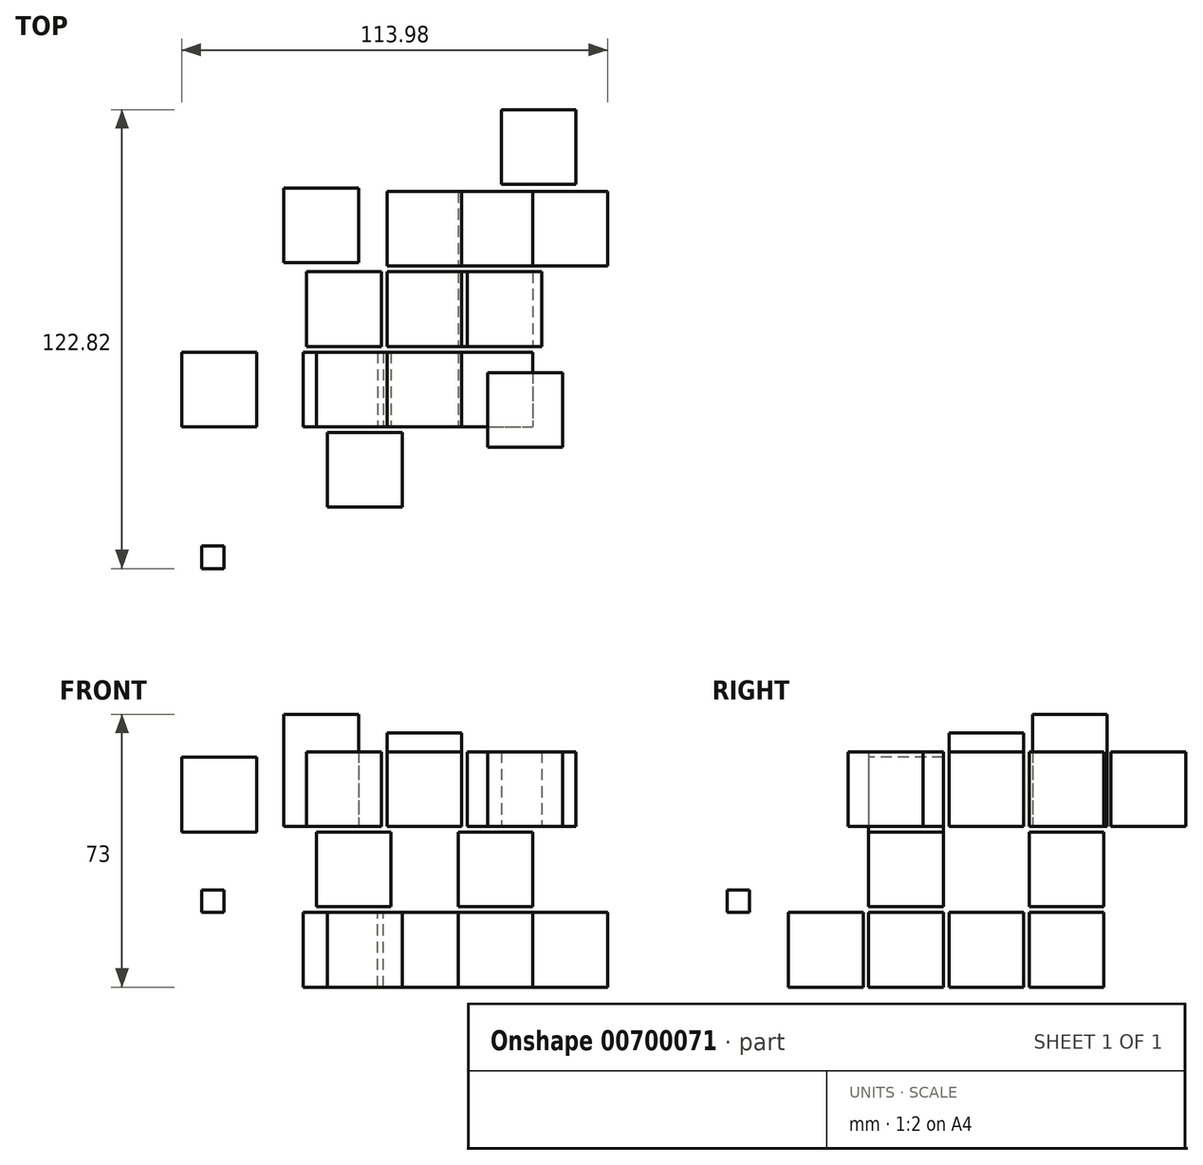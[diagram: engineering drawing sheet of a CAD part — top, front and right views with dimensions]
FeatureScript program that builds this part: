
annotation { "Feature Type Name" : "Feature", "Feature Type Description" : "" }
export const myFeature = defineFeature(function(context is Context, id is Id, definition is map)
    precondition{}
    {
        {
            var Q0;
            Q0=qCreatedBy(makeId("Top.planeOp"),FACE);
            var sketch = newSketch(context, id + "F0", { "sketchPlane" : qUnion([Q0])});
            skLineSegment(sketch, "E0.bottom", {"start": v(-9, -26) * mm, "end": v(11, -26) * mm});
            skLineSegment(sketch, "E0.top", {"start": v(-9, -46) * mm, "end": v(11, -46) * mm});
            skLineSegment(sketch, "E0.left", {"start": v(-9, -26) * mm, "end": v(-9, -46) * mm});
            skLineSegment(sketch, "E0.right", {"start": v(11, -26) * mm, "end": v(11, -46) * mm});
            skLineSegment(sketch, "E1.bottom", {"start": v(-15.53, -4.5) * mm, "end": v(4.47, -4.5) * mm});
            skLineSegment(sketch, "E1.top", {"start": v(-15.53, -24.5) * mm, "end": v(4.47, -24.5) * mm});
            skLineSegment(sketch, "E1.left", {"start": v(-15.53, -4.5) * mm, "end": v(-15.53, -24.5) * mm});
            skLineSegment(sketch, "E1.right", {"start": v(4.47, -4.5) * mm, "end": v(4.47, -24.5) * mm});
            skLineSegment(sketch, "E2.bottom", {"start": v(5.97, -4.5) * mm, "end": v(25.97, -4.5) * mm});
            skLineSegment(sketch, "E2.top", {"start": v(5.97, -24.5) * mm, "end": v(25.97, -24.5) * mm});
            skLineSegment(sketch, "E2.left", {"start": v(5.97, -4.5) * mm, "end": v(5.97, -24.5) * mm});
            skLineSegment(sketch, "E2.right", {"start": v(25.97, -4.5) * mm, "end": v(25.97, -24.5) * mm});
            skLineSegment(sketch, "E3.bottom", {"start": v(25.97, 17) * mm, "end": v(45.97, 17) * mm});
            skLineSegment(sketch, "E3.top", {"start": v(25.97, -3) * mm, "end": v(45.97, -3) * mm});
            skLineSegment(sketch, "E3.left", {"start": v(25.97, 17) * mm, "end": v(25.97, -3) * mm});
            skLineSegment(sketch, "E3.right", {"start": v(45.97, 17) * mm, "end": v(45.97, -3) * mm});
            skLineSegment(sketch, "E4.bottom", {"start": v(45.97, 38.5) * mm, "end": v(65.97, 38.5) * mm});
            skLineSegment(sketch, "E4.top", {"start": v(45.97, 18.5) * mm, "end": v(65.97, 18.5) * mm});
            skLineSegment(sketch, "E4.left", {"start": v(45.97, 38.5) * mm, "end": v(45.97, 18.5) * mm});
            skLineSegment(sketch, "E4.right", {"start": v(65.97, 38.5) * mm, "end": v(65.97, 18.5) * mm});
            skSolve(sketch);
        }
        {
            var Q0;
            Q0=makeQuery(id+"F0.imprint","IMPRINT",FACE,{"disambiguationData":[TD([[makeQuery(id+"F0.imprint","IMPRINT",EDGE,{"derivedFrom":sQuery(id+"F0.wireOp",EDGE,"E0.bottom")}),-1.0]])]});
            var Q1;
            Q1=makeQuery(id+"F0.imprint","IMPRINT",FACE,{"disambiguationData":[TD([[makeQuery(id+"F0.imprint","IMPRINT",EDGE,{"derivedFrom":sQuery(id+"F0.wireOp",EDGE,"E1.bottom")}),-1.0]])]});
            var Q2;
            Q2=makeQuery(id+"F0.imprint","IMPRINT",FACE,{"disambiguationData":[TD([[makeQuery(id+"F0.imprint","IMPRINT",EDGE,{"derivedFrom":sQuery(id+"F0.wireOp",EDGE,"E2.bottom")}),-1.0]])]});
            var Q3;
            Q3=makeQuery(id+"F0.imprint","IMPRINT",FACE,{"disambiguationData":[TD([[makeQuery(id+"F0.imprint","IMPRINT",EDGE,{"derivedFrom":sQuery(id+"F0.wireOp",EDGE,"E3.bottom")}),-1.0]])]});
            var Q4;
            Q4=makeQuery(id+"F0.imprint","IMPRINT",FACE,{"disambiguationData":[TD([[makeQuery(id+"F0.imprint","IMPRINT",EDGE,{"derivedFrom":sQuery(id+"F0.wireOp",EDGE,"E4.bottom")}),-1.0]])]});
            extrude(context, id + "F1", {"entities" : qUnion([Q0, Q1, Q2, Q3, Q4]), "oppositeDirection" : true, "depth" : 20 * mm, "offsetDistance" : 25 * mm});
        }
        {
            var Q0;
            Q0=makeQuery(id+"F1.opExtrude","CAP_FACE",FACE,{"disambiguationData":[OSD([sQuery(id+"F0.wireOp",EDGE,"E0.bottom"),sQuery(id+"F0.wireOp",EDGE,"E0.top"),sQuery(id+"F0.wireOp",EDGE,"E0.left"),sQuery(id+"F0.wireOp",EDGE,"E0.right")])],"isStart":true});
            cPlane(context, id + "F2", {"entities" : qUnion([Q0]), "cplaneType" : CPlaneType.OFFSET, "offset" : 1.5 * mm, "width" : 150 * mm, "height" : 150 * mm});
        }
        {
            var Q0;
            Q0=qCreatedBy(id+"F2.planeOp",FACE);
            var sketch = newSketch(context, id + "F3", { "sketchPlane" : qUnion([Q0])});
            skLineSegment(sketch, "E5.bottom", {"start": v(-12, -4.5) * mm, "end": v(8, -4.5) * mm});
            skLineSegment(sketch, "E5.top", {"start": v(-12, -24.5) * mm, "end": v(8, -24.5) * mm});
            skLineSegment(sketch, "E5.left", {"start": v(-12, -4.5) * mm, "end": v(-12, -24.5) * mm});
            skLineSegment(sketch, "E5.right", {"start": v(8, -4.5) * mm, "end": v(8, -24.5) * mm});
            skLineSegment(sketch, "E6.bottom", {"start": v(25.97, -4.5) * mm, "end": v(45.97, -4.5) * mm});
            skLineSegment(sketch, "E6.top", {"start": v(25.97, -24.5) * mm, "end": v(45.97, -24.5) * mm});
            skLineSegment(sketch, "E6.left", {"start": v(25.97, -4.5) * mm, "end": v(25.97, -24.5) * mm});
            skLineSegment(sketch, "E6.right", {"start": v(45.97, -4.5) * mm, "end": v(45.97, -24.5) * mm});
            skLineSegment(sketch, "E7.bottom", {"start": v(25.97, 38.5) * mm, "end": v(45.97, 38.5) * mm});
            skLineSegment(sketch, "E7.top", {"start": v(25.97, 18.5) * mm, "end": v(45.97, 18.5) * mm});
            skLineSegment(sketch, "E7.left", {"start": v(25.97, 38.5) * mm, "end": v(25.97, 18.5) * mm});
            skLineSegment(sketch, "E7.right", {"start": v(45.97, 38.5) * mm, "end": v(45.97, 18.5) * mm});
            skSolve(sketch);
        }
        {
            var Q0;
            Q0=makeQuery(id+"F3.imprint","IMPRINT",FACE,{"disambiguationData":[TD([[makeQuery(id+"F3.imprint","IMPRINT",EDGE,{"derivedFrom":sQuery(id+"F3.wireOp",EDGE,"E5.bottom")}),-1.0]])]});
            var Q1;
            Q1=makeQuery(id+"F3.imprint","IMPRINT",FACE,{"disambiguationData":[TD([[makeQuery(id+"F3.imprint","IMPRINT",EDGE,{"derivedFrom":sQuery(id+"F3.wireOp",EDGE,"E6.bottom")}),-1.0]])]});
            var Q2;
            Q2=makeQuery(id+"F3.imprint","IMPRINT",FACE,{"disambiguationData":[TD([[makeQuery(id+"F3.imprint","IMPRINT",EDGE,{"derivedFrom":sQuery(id+"F3.wireOp",EDGE,"E7.bottom")}),-1.0]])]});
            extrude(context, id + "F4", {"entities" : qUnion([Q0, Q1, Q2]), "operationType" : NewBodyOperationType.ADD, "depth" : 20 * mm, "offsetDistance" : 25 * mm});
        }
        {
            var Q0;
            Q0=makeQuery(id+"F4.opExtrude","CAP_FACE",FACE,{"disambiguationData":[OSD([sQuery(id+"F3.wireOp",EDGE,"E6.bottom"),sQuery(id+"F3.wireOp",EDGE,"E6.top"),sQuery(id+"F3.wireOp",EDGE,"E6.left"),sQuery(id+"F3.wireOp",EDGE,"E6.right")])],"isStart":false});
            cPlane(context, id + "F5", {"entities" : qUnion([Q0]), "cplaneType" : CPlaneType.OFFSET, "offset" : 1.5 * mm, "width" : 150 * mm, "height" : 150 * mm});
        }
        {
            var Q0;
            Q0=qCreatedBy(id+"F5.planeOp",FACE);
            var sketch = newSketch(context, id + "F6", { "sketchPlane" : qUnion([Q0])});
            skLineSegment(sketch, "E8.bottom", {"start": v(6.9, -4.5) * mm, "end": v(26.9, -4.5) * mm});
            skLineSegment(sketch, "E8.top", {"start": v(6.9, -24.5) * mm, "end": v(26.9, -24.5) * mm});
            skLineSegment(sketch, "E8.left", {"start": v(6.9, -4.5) * mm, "end": v(6.9, -24.5) * mm});
            skLineSegment(sketch, "E8.right", {"start": v(26.9, -4.5) * mm, "end": v(26.9, -24.5) * mm});
            skLineSegment(sketch, "E9.bottom", {"start": v(33.9, -10) * mm, "end": v(53.9, -10) * mm});
            skLineSegment(sketch, "E9.top", {"start": v(33.9, -30) * mm, "end": v(53.9, -30) * mm});
            skLineSegment(sketch, "E9.left", {"start": v(33.9, -10) * mm, "end": v(33.9, -30) * mm});
            skLineSegment(sketch, "E9.right", {"start": v(53.9, -10) * mm, "end": v(53.9, -30) * mm});
            skLineSegment(sketch, "E10.bottom", {"start": v(28.4, 17) * mm, "end": v(48.4, 17) * mm});
            skLineSegment(sketch, "E10.top", {"start": v(28.4, -3) * mm, "end": v(48.4, -3) * mm});
            skLineSegment(sketch, "E10.left", {"start": v(28.4, 17) * mm, "end": v(28.4, -3) * mm});
            skLineSegment(sketch, "E10.right", {"start": v(48.4, 17) * mm, "end": v(48.4, -3) * mm});
            skLineSegment(sketch, "E11.bottom", {"start": v(6.9, 17) * mm, "end": v(26.9, 17) * mm});
            skLineSegment(sketch, "E11.top", {"start": v(6.9, -3) * mm, "end": v(26.9, -3) * mm});
            skLineSegment(sketch, "E11.left", {"start": v(6.9, 17) * mm, "end": v(6.9, -3) * mm});
            skLineSegment(sketch, "E11.right", {"start": v(26.9, 17) * mm, "end": v(26.9, -3) * mm});
            skLineSegment(sketch, "E12.bottom", {"start": v(6.9, 38.5) * mm, "end": v(26.9, 38.5) * mm});
            skLineSegment(sketch, "E12.top", {"start": v(6.9, 18.5) * mm, "end": v(26.9, 18.5) * mm});
            skLineSegment(sketch, "E12.left", {"start": v(6.9, 38.5) * mm, "end": v(6.9, 18.5) * mm});
            skLineSegment(sketch, "E12.right", {"start": v(26.9, 38.5) * mm, "end": v(26.9, 18.5) * mm});
            skLineSegment(sketch, "E13.bottom", {"start": v(-14.6, 17) * mm, "end": v(5.4, 17) * mm});
            skLineSegment(sketch, "E13.top", {"start": v(-14.6, -3) * mm, "end": v(5.4, -3) * mm});
            skLineSegment(sketch, "E13.left", {"start": v(-14.6, 17) * mm, "end": v(-14.6, -3) * mm});
            skLineSegment(sketch, "E13.right", {"start": v(5.4, 17) * mm, "end": v(5.4, -3) * mm});
            skLineSegment(sketch, "E14.bottom", {"start": v(37.52, 60.38) * mm, "end": v(57.52, 60.38) * mm});
            skLineSegment(sketch, "E14.top", {"start": v(37.52, 40.38) * mm, "end": v(57.52, 40.38) * mm});
            skLineSegment(sketch, "E14.left", {"start": v(37.52, 60.38) * mm, "end": v(37.52, 40.38) * mm});
            skLineSegment(sketch, "E14.right", {"start": v(57.52, 60.38) * mm, "end": v(57.52, 40.38) * mm});
            skLineSegment(sketch, "E15.bottom", {"start": v(-20.71, 39.39) * mm, "end": v(-0.71, 39.39) * mm});
            skLineSegment(sketch, "E15.top", {"start": v(-20.71, 19.39) * mm, "end": v(-0.71, 19.39) * mm});
            skLineSegment(sketch, "E15.left", {"start": v(-20.71, 39.39) * mm, "end": v(-20.71, 19.39) * mm});
            skLineSegment(sketch, "E15.right", {"start": v(-0.71, 39.39) * mm, "end": v(-0.71, 19.39) * mm});
            skSolve(sketch);
        }
        {
            var Q0;
            Q0=makeQuery(id+"F6.imprint","IMPRINT",FACE,{"disambiguationData":[TD([[makeQuery(id+"F6.imprint","IMPRINT",EDGE,{"derivedFrom":sQuery(id+"F6.wireOp",EDGE,"E9.bottom")}),-1.0]])]});
            var Q1;
            Q1=makeQuery(id+"F6.imprint","IMPRINT",FACE,{"disambiguationData":[TD([[makeQuery(id+"F6.imprint","IMPRINT",EDGE,{"derivedFrom":sQuery(id+"F6.wireOp",EDGE,"E8.bottom")}),-1.0]])]});
            var Q2;
            Q2=makeQuery(id+"F6.imprint","IMPRINT",FACE,{"disambiguationData":[TD([[makeQuery(id+"F6.imprint","IMPRINT",EDGE,{"derivedFrom":sQuery(id+"F6.wireOp",EDGE,"E13.bottom")}),-1.0]])]});
            var Q3;
            Q3=makeQuery(id+"F6.imprint","IMPRINT",FACE,{"disambiguationData":[TD([[makeQuery(id+"F6.imprint","IMPRINT",EDGE,{"derivedFrom":sQuery(id+"F6.wireOp",EDGE,"E12.bottom")}),-1.0]])]});
            var Q4;
            Q4=makeQuery(id+"F6.imprint","IMPRINT",FACE,{"disambiguationData":[TD([[makeQuery(id+"F6.imprint","IMPRINT",EDGE,{"derivedFrom":sQuery(id+"F6.wireOp",EDGE,"E14.bottom")}),-1.0]])]});
            extrude(context, id + "F7", {"entities" : qUnion([Q0, Q1, Q2, Q3, Q4]), "depth" : 20 * mm, "offsetDistance" : 25 * mm});
        }
        {
            var Q0;
            Q0=makeQuery(id+"F6.imprint","IMPRINT",FACE,{"disambiguationData":[TD([[makeQuery(id+"F6.imprint","IMPRINT",EDGE,{"derivedFrom":sQuery(id+"F6.wireOp",EDGE,"E11.bottom")}),-1.0]])]});
            extrude(context, id + "F8", {"entities" : qUnion([Q0]), "depth" : 25 * mm, "offsetDistance" : 25 * mm});
        }
        {
            var Q0;
            Q0=makeQuery(id+"F6.imprint","IMPRINT",FACE,{"disambiguationData":[TD([[makeQuery(id+"F6.imprint","IMPRINT",EDGE,{"derivedFrom":sQuery(id+"F6.wireOp",EDGE,"E10.bottom")}),-1.0]])]});
            extrude(context, id + "F9", {"entities" : qUnion([Q0]), "depth" : 20 * mm, "offsetDistance" : 25 * mm});
        }
        {
            var Q0;
            Q0=makeQuery(id+"F6.imprint","IMPRINT",FACE,{"disambiguationData":[TD([[makeQuery(id+"F6.imprint","IMPRINT",EDGE,{"derivedFrom":sQuery(id+"F6.wireOp",EDGE,"E15.bottom")}),-1.0]])]});
            extrude(context, id + "F10", {"entities" : qUnion([Q0]), "depth" : 30 * mm, "offsetDistance" : 25 * mm});
        }
        {
            var Q0;
            Q0=makeQuery(id+"F1.opExtrude","CAP_FACE",FACE,{"disambiguationData":[OSD([sQuery(id+"F0.wireOp",EDGE,"E0.bottom"),sQuery(id+"F0.wireOp",EDGE,"E0.top"),sQuery(id+"F0.wireOp",EDGE,"E0.left"),sQuery(id+"F0.wireOp",EDGE,"E0.right")])],"isStart":true});
            var sketch = newSketch(context, id + "F11", { "sketchPlane" : qUnion([Q0])});
            skLineSegment(sketch, "E16.bottom", {"start": v(-42.7, -56.44) * mm, "end": v(-36.7, -56.44) * mm});
            skLineSegment(sketch, "E16.top", {"start": v(-42.7, -62.44) * mm, "end": v(-36.7, -62.44) * mm});
            skLineSegment(sketch, "E16.left", {"start": v(-42.7, -56.44) * mm, "end": v(-42.7, -62.44) * mm});
            skLineSegment(sketch, "E16.right", {"start": v(-36.7, -56.44) * mm, "end": v(-36.7, -62.44) * mm});
            skSolve(sketch);
        }
        {
            var Q0;
            Q0=makeQuery(id+"F11.imprint","IMPRINT",FACE,{"disambiguationData":[TD([[makeQuery(id+"F11.imprint","IMPRINT",EDGE,{"derivedFrom":sQuery(id+"F11.wireOp",EDGE,"E16.bottom")}),-1.0]])]});
            extrude(context, id + "F12", {"entities" : qUnion([Q0]), "depth" : 6 * mm, "offsetDistance" : 25 * mm});
        }
        {
            var Q0;
            Q0=makeQuery(id+"F4.opExtrude","CAP_FACE",FACE,{"disambiguationData":[OSD([sQuery(id+"F3.wireOp",EDGE,"E5.bottom"),sQuery(id+"F3.wireOp",EDGE,"E5.top"),sQuery(id+"F3.wireOp",EDGE,"E5.left"),sQuery(id+"F3.wireOp",EDGE,"E5.right")])],"isStart":false});
            var sketch = newSketch(context, id + "F13", { "sketchPlane" : qUnion([Q0])});
            skLineSegment(sketch, "E17.bottom", {"start": v(-48, -4.5) * mm, "end": v(-28, -4.5) * mm});
            skLineSegment(sketch, "E17.top", {"start": v(-48, -24.5) * mm, "end": v(-28, -24.5) * mm});
            skLineSegment(sketch, "E17.left", {"start": v(-48, -4.5) * mm, "end": v(-48, -24.5) * mm});
            skLineSegment(sketch, "E17.right", {"start": v(-28, -4.5) * mm, "end": v(-28, -24.5) * mm});
            skSolve(sketch);
        }
        {
            var Q0;
            Q0=makeQuery(id+"F13.imprint","IMPRINT",FACE,{"disambiguationData":[TD([[makeQuery(id+"F13.imprint","IMPRINT",EDGE,{"derivedFrom":sQuery(id+"F13.wireOp",EDGE,"E17.bottom")}),-1.0]])]});
            extrude(context, id + "F14", {"entities" : qUnion([Q0]), "depth" : 20 * mm, "offsetDistance" : 25 * mm});
        }
    });
